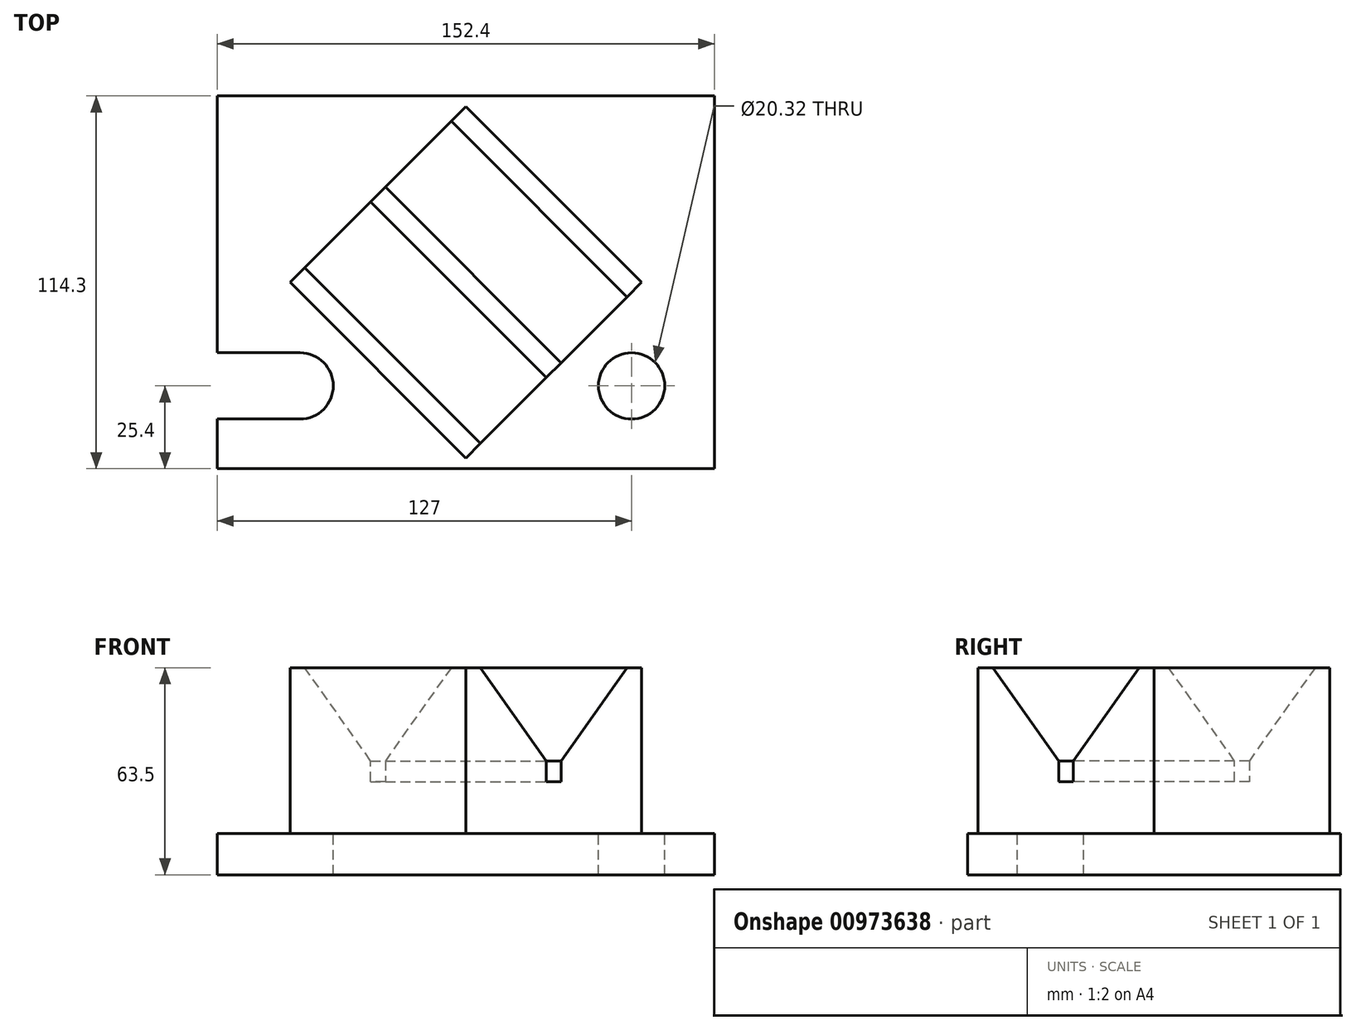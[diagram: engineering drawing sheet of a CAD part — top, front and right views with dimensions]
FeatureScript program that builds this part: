
annotation { "Feature Type Name" : "Feature", "Feature Type Description" : "" }
export const myFeature = defineFeature(function(context is Context, id is Id, definition is map)
    precondition{}
    {
        {
            var Q0;
            Q0=qCreatedBy(makeId("Top.planeOp"),FACE);
            var sketch = newSketch(context, id + "F0", { "sketchPlane" : qUnion([Q0])});
            skLineSegment(sketch, "E0.bottom", {"start": v(-76.2, 57.15) * mm, "end": v(76.2, 57.15) * mm});
            skLineSegment(sketch, "E0.top", {"start": v(-76.2, -57.15) * mm, "end": v(76.2, -57.15) * mm});
            skLineSegment(sketch, "E0.left", {"start": v(-76.2, 57.15) * mm, "end": v(-76.2, -57.15) * mm});
            skLineSegment(sketch, "E0.right", {"start": v(76.2, 57.15) * mm, "end": v(76.2, -57.15) * mm});
            skPoint(sketch, "E0.middle", {"position": v(0, 0) * mm});
            skSolve(sketch);
        }
        {
            var Q0;
            Q0=makeQuery(id+"F0.imprint","IMPRINT",FACE,{"disambiguationData":[TD([[makeQuery(id+"F0.imprint","IMPRINT",EDGE,{"derivedFrom":sQuery(id+"F0.wireOp",EDGE,"E0.bottom")}),-1.0]])]});
            extrude(context, id + "F1", {"entities" : qUnion([Q0]), "depth" : 12.7 * mm, "offsetDistance" : 25.4 * mm});
        }
        {
            var Q0;
            Q0=makeQuery(id+"F1.opExtrude","CAP_FACE",FACE,{"disambiguationData":[OSD([sQuery(id+"F0.wireOp",EDGE,"E0.bottom"),sQuery(id+"F0.wireOp",EDGE,"E0.top"),sQuery(id+"F0.wireOp",EDGE,"E0.left"),sQuery(id+"F0.wireOp",EDGE,"E0.right")])],"isStart":false});
            var sketch = newSketch(context, id + "F2", { "sketchPlane" : qUnion([Q0])});
            skLineSegment(sketch, "E1", {"start": v(-76.2, -21.59) * mm, "end": v(-50.8, -21.59) * mm});
            skLineSegment(sketch, "E2", {"start": v(-76.2, -41.91) * mm, "end": v(-50.8, -41.91) * mm});
            skArc(sketch, "E3", {"start": v(-50.8, -41.91) * mm, "mid": v(-40.64, -31.75) * mm, "end": v(-50.8, -21.59) * mm});
            skSolve(sketch);
        }
        {
            var Q0;
            Q0 = qSketchRegion(id + "F2", true);
            var Q1;
            {var subQ0=sQuery(id+"F2.wireOp",EDGE,"E1");Q1=makeQuery(id+"F2.imprint","IMPRINT",FACE,{"disambiguationData":[TD([[makeQuery(id+"F2.imprint","IMPRINT",EDGE,{"derivedFrom":subQ0}),-1.0]])]});}
            var Q2;
            Q2=makeQuery(id+"F1.opExtrude","CAP_FACE",FACE,{"disambiguationData":[OSD([sQuery(id+"F0.wireOp",EDGE,"E0.bottom"),sQuery(id+"F0.wireOp",EDGE,"E0.top"),sQuery(id+"F0.wireOp",EDGE,"E0.left"),sQuery(id+"F0.wireOp",EDGE,"E0.right")])],"isStart":true});
            extrude(context, id + "F3", {"entities" : qUnion([Q0, Q1]), "operationType" : NewBodyOperationType.REMOVE, "endBound" : BoundingType.UP_TO_SURFACE, "oppositeDirection" : true, "depth" : 44.7 * mm, "endBoundEntityFace" : qUnion([Q2]), "offsetDistance" : 25.4 * mm});
        }
        {
            var Q0;
            Q0=makeQuery(id+"F1.opExtrude","CAP_FACE",FACE,{"disambiguationData":[OSD([sQuery(id+"F0.wireOp",EDGE,"E0.bottom"),sQuery(id+"F0.wireOp",EDGE,"E0.top"),sQuery(id+"F0.wireOp",EDGE,"E0.left"),sQuery(id+"F0.wireOp",EDGE,"E0.right")])],"isStart":false});
            var sketch = newSketch(context, id + "F4", { "sketchPlane" : qUnion([Q0])});
            skCircle(sketch, "E4", {"center": v(50.8, -31.75) * mm, "radius": 10.16 * mm});
            skSolve(sketch);
        }
        {
            var Q0;
            Q0=makeQuery(id+"F4.imprint","IMPRINT",FACE,{"disambiguationData":[TD([[makeQuery(id+"F4.imprint","IMPRINT",EDGE,{"derivedFrom":sQuery(id+"F4.wireOp",EDGE,"E4")}),1.0]])]});
            var Q1;
            Q1=makeQuery(id+"F1.opExtrude","CAP_FACE",FACE,{"disambiguationData":[OSD([sQuery(id+"F0.wireOp",EDGE,"E0.bottom"),sQuery(id+"F0.wireOp",EDGE,"E0.top"),sQuery(id+"F0.wireOp",EDGE,"E0.left"),sQuery(id+"F0.wireOp",EDGE,"E0.right")])],"isStart":true});
            extrude(context, id + "F5", {"entities" : qUnion([Q0]), "operationType" : NewBodyOperationType.REMOVE, "endBound" : BoundingType.UP_TO_SURFACE, "oppositeDirection" : true, "depth" : 25.4 * mm, "endBoundEntityFace" : qUnion([Q1]), "offsetDistance" : 25.4 * mm});
        }
        {
            var Q0;
            Q0=makeQuery(id+"F1.opExtrude","CAP_FACE",FACE,{"disambiguationData":[OSD([sQuery(id+"F0.wireOp",EDGE,"E0.bottom"),sQuery(id+"F0.wireOp",EDGE,"E0.top"),sQuery(id+"F0.wireOp",EDGE,"E0.left"),sQuery(id+"F0.wireOp",EDGE,"E0.right")])],"isStart":false});
            var sketch = newSketch(context, id + "F6", { "sketchPlane" : qUnion([Q0])});
            skLineSegment(sketch, "E5.bottom", {"start": v(0, 53.88) * mm, "end": v(53.88, 0) * mm});
            skLineSegment(sketch, "E5.top", {"start": v(-53.88, 0) * mm, "end": v(0, -53.88) * mm});
            skLineSegment(sketch, "E5.left", {"start": v(0, 53.88) * mm, "end": v(-53.88, 0) * mm});
            skLineSegment(sketch, "E5.right", {"start": v(53.88, 0) * mm, "end": v(0, -53.88) * mm});
            skSolve(sketch);
        }
        {
            var Q0;
            Q0=makeQuery(id+"F6.imprint","IMPRINT",FACE,{"disambiguationData":[TD([[makeQuery(id+"F6.imprint","IMPRINT",EDGE,{"derivedFrom":sQuery(id+"F6.wireOp",EDGE,"E5.bottom")}),-1.0]])]});
            extrude(context, id + "F7", {"entities" : qUnion([Q0]), "operationType" : NewBodyOperationType.ADD, "depth" : 50.8 * mm, "offsetDistance" : 25.4 * mm});
        }
        {
            var Q0;
            Q0=makeQuery(id+"F7.opExtrude","SWEPT_FACE",FACE,{"disambiguationData":[OSD([sQuery(id+"F6.wireOp",EDGE,"E5.right")])]});
            var sketch = newSketch(context, id + "F8", { "sketchPlane" : qUnion([Q0])});
            skLineSegment(sketch, "E6", {"start": v(-31.75, 63.5) * mm, "end": v(-3.18, 34.93) * mm});
            skLineSegment(sketch, "E7", {"start": v(-3.18, 34.93) * mm, "end": v(-3.18, 28.58) * mm});
            skLineSegment(sketch, "E8", {"start": v(-3.18, 28.58) * mm, "end": v(3.18, 28.58) * mm});
            skLineSegment(sketch, "E9", {"start": v(3.18, 28.58) * mm, "end": v(3.18, 34.93) * mm});
            skLineSegment(sketch, "E10", {"start": v(3.17, 34.92) * mm, "end": v(31.75, 63.5) * mm});
            skLineSegment(sketch, "E11", {"start": v(0, 12.7) * mm, "end": v(0, 28.58) * mm, "construction": true});
            skSolve(sketch);
        }
        {
            var Q0;
            {var subQ0=sQuery(id+"F8.wireOp",EDGE,"E6");Q0=makeQuery(id+"F8.imprint","IMPRINT",FACE,{"disambiguationData":[TD([[makeQuery(id+"F8.imprint","IMPRINT",EDGE,{"derivedFrom":subQ0}),1.0]])]});}
            var Q1;
            Q1=makeQuery(id+"F7.opExtrude","SWEPT_FACE",FACE,{"disambiguationData":[OSD([sQuery(id+"F6.wireOp",EDGE,"E5.left")])]});
            extrude(context, id + "F9", {"entities" : qUnion([Q0]), "operationType" : NewBodyOperationType.REMOVE, "endBound" : BoundingType.UP_TO_SURFACE, "oppositeDirection" : true, "depth" : 25.4 * mm, "endBoundEntityFace" : qUnion([Q1]), "offsetDistance" : 25.4 * mm});
        }
    });
